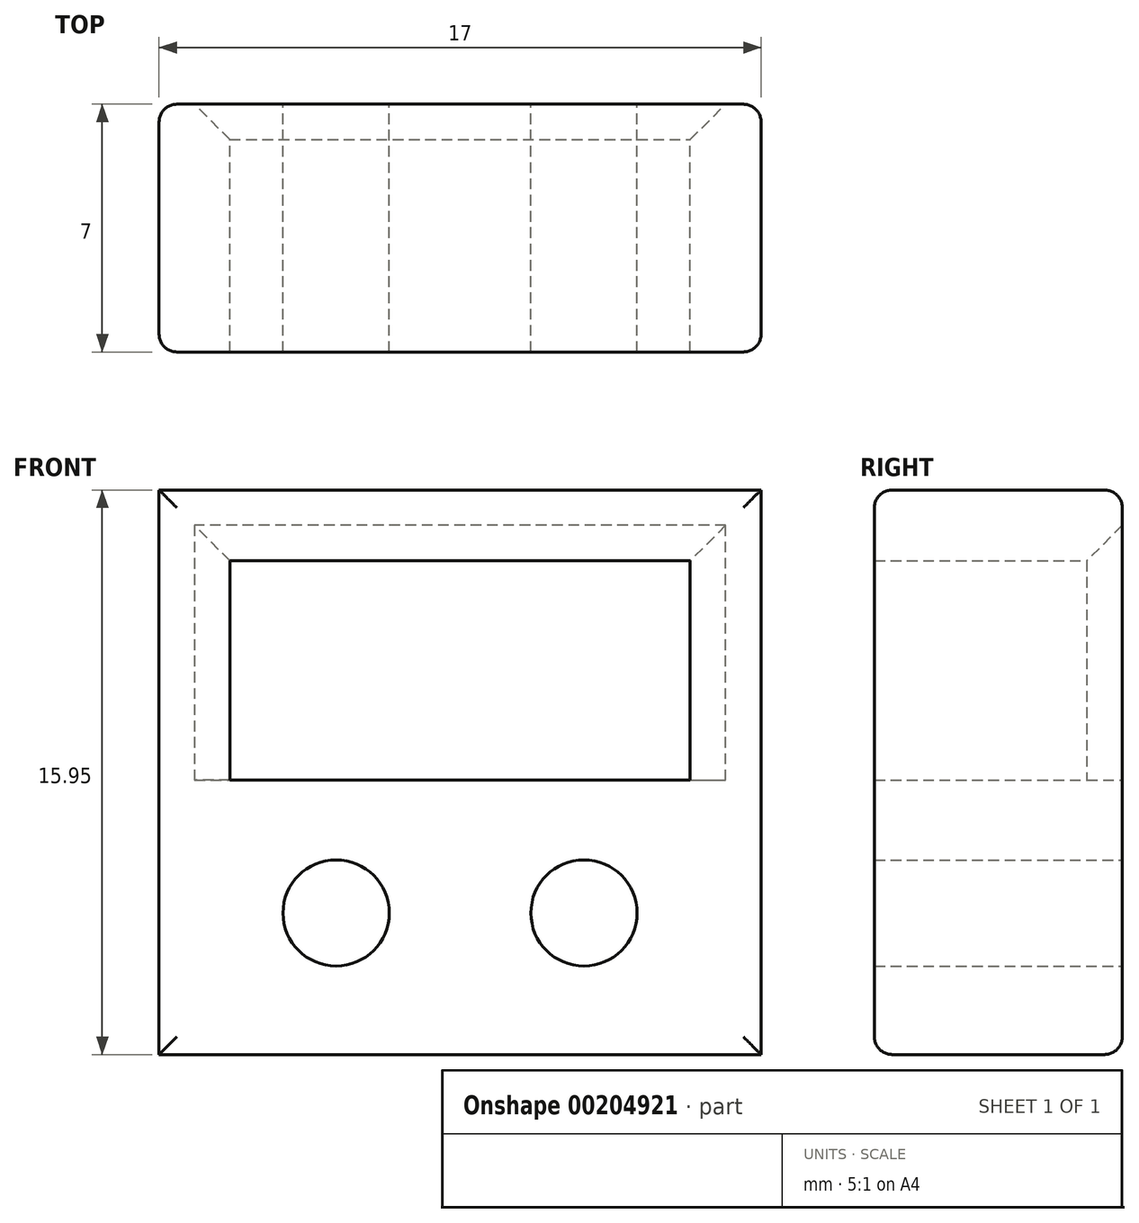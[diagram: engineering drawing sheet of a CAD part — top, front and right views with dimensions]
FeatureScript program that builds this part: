
annotation { "Feature Type Name" : "Feature", "Feature Type Description" : "" }
export const myFeature = defineFeature(function(context is Context, id is Id, definition is map)
    precondition{}
    {
        {
            var Q0;
            Q0=qCreatedBy(makeId("Front.planeOp"),FACE);
            var sketch = newSketch(context, id + "F0", { "sketchPlane" : qUnion([Q0])});
            skLineSegment(sketch, "E0.bottom", {"start": v(0, 0) * mm, "end": v(17, 0) * mm});
            skLineSegment(sketch, "E0.top", {"start": v(0, 7.75) * mm, "end": v(17, 7.75) * mm});
            skLineSegment(sketch, "E0.left", {"start": v(0, 0) * mm, "end": v(0, 7.75) * mm});
            skLineSegment(sketch, "E0.right", {"start": v(17, 0) * mm, "end": v(17, 7.75) * mm});
            skLineSegment(sketch, "E1", {"start": v(0, 4) * mm, "end": v(17, 4) * mm, "construction": true});
            skCircle(sketch, "E2", {"center": v(5, 4) * mm, "radius": 1.5 * mm});
            skCircle(sketch, "E3", {"center": v(12, 4) * mm, "radius": 1.5 * mm});
            skLineSegment(sketch, "E4.bottom", {"start": v(2, 7.75) * mm, "end": v(15, 7.75) * mm});
            skLineSegment(sketch, "E4.top", {"start": v(2, 13.95) * mm, "end": v(15, 13.95) * mm});
            skLineSegment(sketch, "E4.left", {"start": v(2, 7.75) * mm, "end": v(2, 13.95) * mm});
            skLineSegment(sketch, "E4.right", {"start": v(15, 7.75) * mm, "end": v(15, 13.95) * mm});
            skLineSegment(sketch, "E5.bottom", {"start": v(0, 7.75) * mm, "end": v(17, 7.75) * mm, "construction": true});
            skLineSegment(sketch, "E5.top", {"start": v(0, 15.95) * mm, "end": v(17, 15.95) * mm});
            skLineSegment(sketch, "E5.left", {"start": v(0, 7.75) * mm, "end": v(0, 15.95) * mm});
            skLineSegment(sketch, "E5.right", {"start": v(17, 7.75) * mm, "end": v(17, 15.95) * mm});
            skLineSegment(sketch, "E6", {"start": v(2, 13.95) * mm, "end": v(2, 15.95) * mm, "construction": true});
            skLineSegment(sketch, "E7", {"start": v(2, 13.95) * mm, "end": v(0, 13.95) * mm, "construction": true});
            skLineSegment(sketch, "E8", {"start": v(15, 13.95) * mm, "end": v(17, 13.95) * mm, "construction": true});
            skSolve(sketch);
        }
        {
            var Q0;
            Q0=makeQuery(id+"F0.imprint","IMPRINT",FACE,{"disambiguationData":[TD([[makeQuery(id+"F0.imprint","IMPRINT",EDGE,{"derivedFrom":sQuery(id+"F0.wireOp",EDGE,"E0.bottom")}),1.0]])]});
            var Q1;
            Q1=makeQuery(id+"F0.imprint","IMPRINT",FACE,{"disambiguationData":[TD([[makeQuery(id+"F0.imprint","IMPRINT",EDGE,{"derivedFrom":sQuery(id+"F0.wireOp",EDGE,"E4.top")}),1.0]])]});
            extrude(context, id + "F1", {"entities" : qUnion([Q0, Q1]), "depth" : 7 * mm});
        }
        {
            var Q0;
            Q0=makeQuery(id+"F1.opExtrude","CAP_EDGE",EDGE,{"disambiguationData":[OSD([sQuery(id+"F0.wireOp",EDGE,"E4.bottom")])],"isStart":true});
            var Q1;
            Q1=makeQuery(id+"F1.opExtrude","CAP_EDGE",EDGE,{"disambiguationData":[OSD([sQuery(id+"F0.wireOp",EDGE,"E4.left")])],"isStart":true});
            var Q2;
            Q2=makeQuery(id+"F1.opExtrude","CAP_EDGE",EDGE,{"disambiguationData":[OSD([sQuery(id+"F0.wireOp",EDGE,"E4.top")])],"isStart":true});
            var Q3;
            Q3=makeQuery(id+"F1.opExtrude","CAP_EDGE",EDGE,{"disambiguationData":[OSD([sQuery(id+"F0.wireOp",EDGE,"E4.right")])],"isStart":true});
            chamfer(context, id + "F2", {"entities" : qUnion([Q0, Q1, Q2, Q3]), "width" : 1 * mm, "tangentPropagation" : true});
        }
        {
            var Q0;
            Q0=makeQuery(id+"F1.opExtrude","CAP_EDGE",EDGE,{"disambiguationData":[OSD([sQuery(id+"F0.wireOp",EDGE,"E0.bottom")])],"isStart":false});
            var Q1;
            Q1=makeQuery(id+"F1.opExtrude","CAP_EDGE",EDGE,{"disambiguationData":[OSD([sQuery(id+"F0.wireOp",EDGE,"E0.right"),sQuery(id+"F0.wireOp",EDGE,"E5.right")])],"isStart":false});
            var Q2;
            Q2=makeQuery(id+"F1.opExtrude","CAP_EDGE",EDGE,{"disambiguationData":[OSD([sQuery(id+"F0.wireOp",EDGE,"E5.top")])],"isStart":false});
            var Q3;
            Q3=makeQuery(id+"F1.opExtrude","CAP_EDGE",EDGE,{"disambiguationData":[OSD([sQuery(id+"F0.wireOp",EDGE,"E0.left"),sQuery(id+"F0.wireOp",EDGE,"E5.left")])],"isStart":false});
            var Q4;
            Q4=makeQuery(id+"F1.opExtrude","CAP_EDGE",EDGE,{"disambiguationData":[OSD([sQuery(id+"F0.wireOp",EDGE,"E0.right"),sQuery(id+"F0.wireOp",EDGE,"E5.right")])],"isStart":true});
            var Q5;
            Q5=makeQuery(id+"F1.opExtrude","CAP_EDGE",EDGE,{"disambiguationData":[OSD([sQuery(id+"F0.wireOp",EDGE,"E0.bottom")])],"isStart":true});
            var Q6;
            Q6=makeQuery(id+"F1.opExtrude","CAP_EDGE",EDGE,{"disambiguationData":[OSD([sQuery(id+"F0.wireOp",EDGE,"E0.left"),sQuery(id+"F0.wireOp",EDGE,"E5.left")])],"isStart":true});
            var Q7;
            Q7=makeQuery(id+"F1.opExtrude","CAP_EDGE",EDGE,{"disambiguationData":[OSD([sQuery(id+"F0.wireOp",EDGE,"E5.top")])],"isStart":true});
            fillet(context, id + "F3", {"entities" : qUnion([Q0, Q1, Q2, Q3, Q4, Q5, Q6, Q7]), "radius" : .5 * mm, "tangentPropagation" : true, "allowEdgeOverflow" : false});
        }
    });
